# Revit family: Countertop-Supports_Centerline-Brackets_Island-Support-System
name_source: partatom
category: Casework
units: mm (PartAtom-declared; Revit-internal decimal feet)

## family parameters
Always vertical = Yes
Classification Number = 23.40.35.11
Cut with Voids When Loaded = No
Room Calculation Point = No
Shared = No
Work Plane-Based = No

## types (1)
- ISS
    Assembly Code = E2010200
    Default Elevation = 0"
    Description = Island Support Bracket System
    Finish = Available Powder Coat Finishes; White (W), Black (B)
    Finish Note = When choosing an alternative finish, please remember to update the model number to reflect the chosen finish.
    Height = 1/2"
    Keynote = 12000
    Manufacturer = Centerline Brackets
    Model = ISS-B
    Product Material = Centerline Brackets - Steel - Powder Coated - Black (B)
    Product data url = https://www.bimobject.com
    URL = https://www.countertopbracket.com

## geometry (parser evidence)
native form markers: Sweep x10
no freeform markers — native parametric forms only
